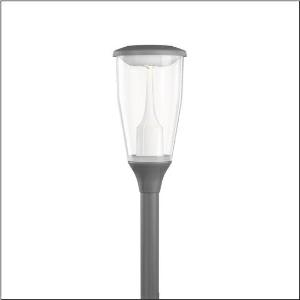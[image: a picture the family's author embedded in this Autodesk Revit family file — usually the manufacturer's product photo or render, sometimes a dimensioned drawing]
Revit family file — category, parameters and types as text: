
# Revit family: dl_11_iq___p1_0a_5xa5565nf14h000022_7674
name_source: partatom
category: Lighting Fixtures
units: mm (PartAtom-declared; Revit-internal decimal feet)

## family parameters
Cut with Voids When Loaded = No
Host = Face
Light Source = No
Part Type = Normal
Room Calculation Point = No
Round Connector Dimension = Use Diameter
Shared = No

## types (1)
- --- (1 x LED, 1530 lm, 11.8 W, 2700K)
    Apparent Load = 12 VA
    CIE Flux Codes = 34 63 91 95 100
    Color Rendering = 70
    Color Temperature = 2700K
    Default Elevation = 1800 mm
    Description = DL 11 iQ, mast luminaire, Module 540 iQ-SR, primary light control with 3 zone facetted reflector, of plastic, silver coated, highly specular, structured, primary optical cover: cover, of PMMA, transparent, light distribution: P1.0a, light emission: direct distribution, primary light characteristic: asymmetric, installation type: post-top, LED, High Power LED, rated luminous flux: 1.560lm, luminous efficacy: 149lm/W, light colour: 727, colour temperature: 2700K, control: Street-Remote, Auto-Match, Temp-Guard, Lumen-Switch, Night-Set, Smart-Wire, Light-Fading, Desk-Remote (wireless, voltage-free reading and setting of iQ features in the workshop via application-optimized NFC function/RFID function), optimised constant luminous flux control (CLO 2.0), mains connection: 220..240V, AC, 50/60Hz, connection cable pre-assembled, cable length: 5,5m, start of lifetime: 12W, end of service life: 12W, reduction: 5W, luminaire housing, upper part, of diecast aluminium, coated, Siteco® metallic grey (DB 702S), spigot size: 60mm (post-top), post-top mast mounting element, of diecast aluminium, coated, Siteco® metallic grey (DB 702S), Module 540 iQ-SR, traffic white (RAL 9016), equipment: standard, protection rating (complete): IP66, insulation class (complete): insulation class II (safety insulation), certification: CE, ENEC, ENEC+, VDE, packaging unit: 1 piece

Light Distribution: P1.0a
    Height = 665 mm
    Lamp = 1 x LED
    Lamp Light Flux = 1530 lm
    Lamp Power = 11.8 W
    Lamp count = 1
    Length = 334 mm
    Luminous efficacy = 130 lm/W
    Manufacturer = Siteco
    ModVariant = No
    Model = 5XA5565NF14H000022
    Number of Poles = 1
    OnlyDefault = Yes
    Power Factor = 1
    Product Name = DL 11 iQ | P1.0a
    Product group = mast luminaire | pylon top
    ProductGroupID = 6100
    Protection Class = Protection class II
    Protection Degree = IP 66
    RLX_Detail_Level = 1
    RLX_Emergency_Light_Flux = 0 lm
    RLX_Emergency_Type = 0
    RLX_Emergency_Type_DB = No
    RlxData = <blob elided: 103749 chars, md5=b6c4d4ae>
    Socket = socket
    Standby Power = 0 W
    System Light Flux = 1530 lm
    System Power = 12 W
    Type Comments = factory setting: luminous flux: 100 % | dim-lin: 254 | 472 mA
    Type Image = l_1258354.jpg
    URL = http://relux.com
    VarID = @adj_042373
    Voltage = 0 V
    Weight = 0.00 kg
    Width = 0 mm  [stored 0 ft]

note: [stored X ft] marks values corroborated as IEEE doubles in the binary element streams (Revit-internal decimal feet)

## geometry (parser evidence)
native form markers: Blend x4, Sweep x11
no freeform markers — native parametric forms only
